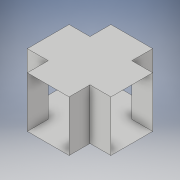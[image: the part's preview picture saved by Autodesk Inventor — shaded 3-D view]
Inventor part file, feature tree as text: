
AUTODESK INVENTOR PART (.ipt)
format: ipt  version: 2017 (Build 210142000, 142)  size: 109,056 bytes
history: native  units: in
note: dims shown in document units (in); Inventor stores cm internally (conversion verified against a paired STEP export)
features: extrude x1, pattern_circular x1, delete_face x1, sketch x1
ambient origin geometry x8: Origin, YZ Plane, XZ Plane, XY Plane, X Axis, Y Axis, Z Axis, Center Point
bodies: Solid1 (feature_tree)
feature tree (4):
  extrude  "Extrusion1"  Depth=8.5in
  pattern_circular  "Circular Pattern1"  [2 undecoded]
  delete_face  "Delete Face1"
  sketch  "Sketch1"  dims[d0=7.0in d1=8.5in d2=7.0in d3=0.0in d4=1.5748in d5=360.0deg]
note: 2 required parameter values undecoded (feature->parameter linkage not recoverable at this tier; creation-order binding heuristic only, values carry confidence <= 0.55)
